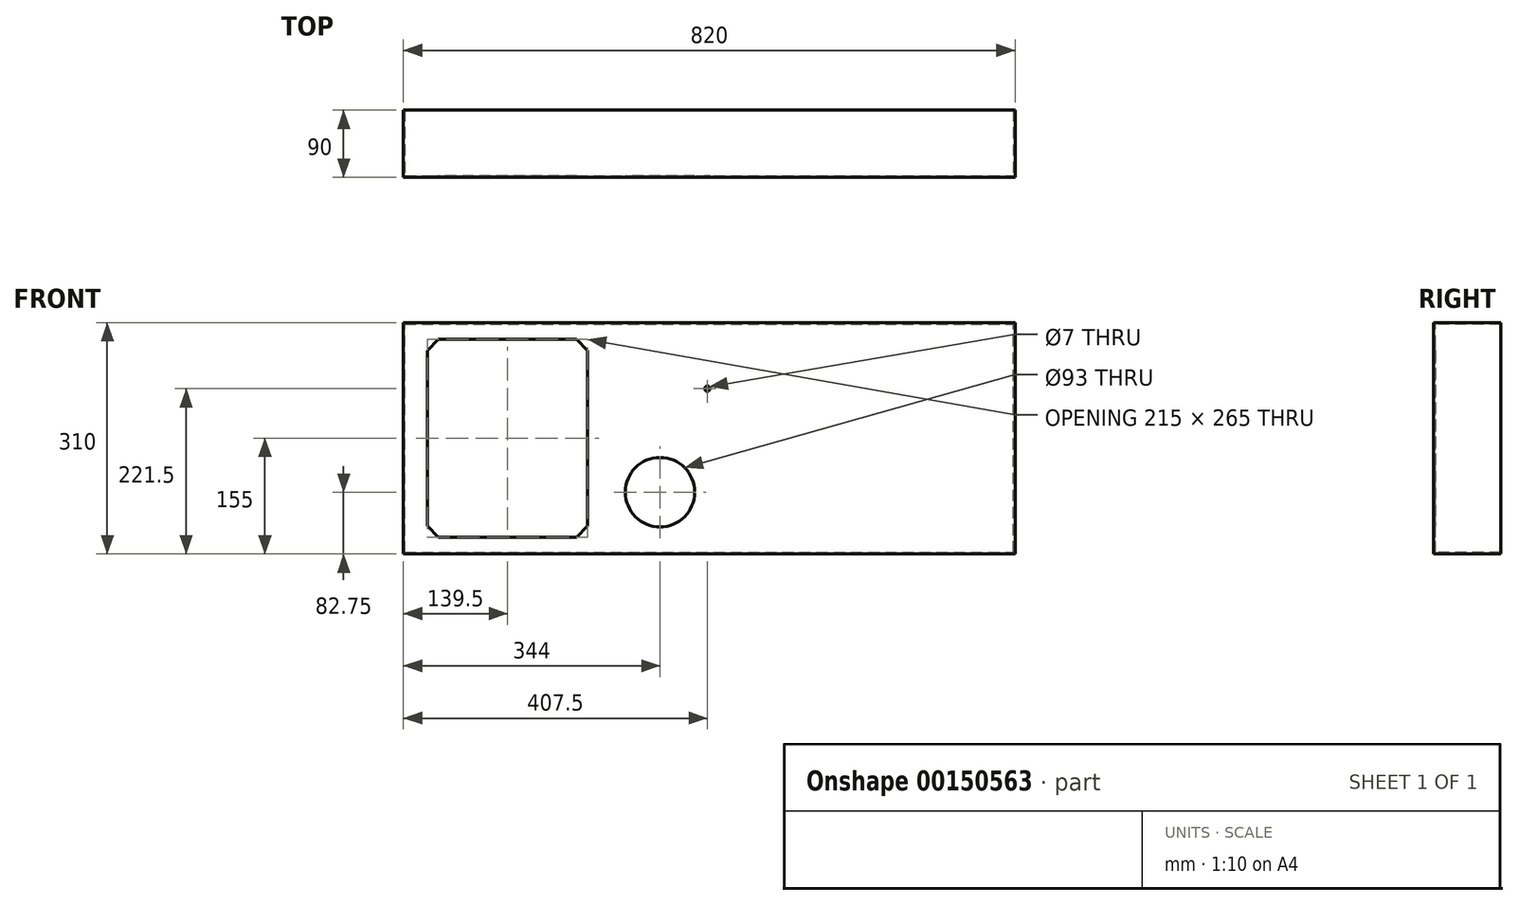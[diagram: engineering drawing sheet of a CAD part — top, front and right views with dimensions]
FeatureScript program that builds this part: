
annotation { "Feature Type Name" : "Feature", "Feature Type Description" : "" }
export const myFeature = defineFeature(function(context is Context, id is Id, definition is map)
    precondition{}
    {
        {
            var Q0;
            Q0=qCreatedBy(makeId("Front.planeOp"),FACE);
            var sketch = newSketch(context, id + "F0", { "sketchPlane" : qUnion([Q0])});
            skLineSegment(sketch, "E0.bottom", {"start": v(0, 0) * mm, "end": v(820, 0) * mm});
            skLineSegment(sketch, "E0.top", {"start": v(0, 310) * mm, "end": v(820, 310) * mm});
            skLineSegment(sketch, "E0.left", {"start": v(0, 0) * mm, "end": v(0, 310) * mm});
            skLineSegment(sketch, "E0.right", {"start": v(820, 0) * mm, "end": v(820, 310) * mm});
            skSolve(sketch);
        }
        {
            var Q0;
            Q0 = qSketchRegion(id + "F0", true);
            extrude(context, id + "F1", {"entities" : qUnion([Q0]), "depth" : 2 * mm});
        }
        {
            var Q0;
            Q0=makeQuery(id+"F1.opExtrude","CAP_FACE",FACE,{"disambiguationData":[OSD([sQuery(id+"F0.wireOp",EDGE,"E0.bottom"),sQuery(id+"F0.wireOp",EDGE,"E0.top"),sQuery(id+"F0.wireOp",EDGE,"E0.left"),sQuery(id+"F0.wireOp",EDGE,"E0.right")])],"isStart":true});
            var sketch = newSketch(context, id + "F2", { "sketchPlane" : qUnion([Q0])});
            skLineSegment(sketch, "E1.0", {"start": v(-820, 0) * mm, "end": v(-820, 310) * mm});
            skLineSegment(sketch, "E1.1", {"start": v(0, 310) * mm, "end": v(-820, 310) * mm});
            skLineSegment(sketch, "E1.2", {"start": v(0, 0) * mm, "end": v(-820, 0) * mm});
            skLineSegment(sketch, "E1.3", {"start": v(0, 0) * mm, "end": v(0, 310) * mm});
            skLineSegment(sketch, "E2.0", {"start": v(-818, 2) * mm, "end": v(-818, 308) * mm});
            skLineSegment(sketch, "E2.1", {"start": v(-2, 2) * mm, "end": v(-818, 2) * mm});
            skLineSegment(sketch, "E2.2", {"start": v(-2, 2) * mm, "end": v(-2, 308) * mm});
            skLineSegment(sketch, "E2.3", {"start": v(-2, 308) * mm, "end": v(-818, 308) * mm});
            skSolve(sketch);
        }
        {
            var Q0;
            Q0 = qSketchRegion(id + "F2", true);
            extrude(context, id + "F3", {"entities" : qUnion([Q0]), "operationType" : NewBodyOperationType.ADD, "depth" : 88 * mm});
        }
        {
            var Q0;
            Q0=makeQuery(id+"F1.opExtrude","CAP_FACE",FACE,{"disambiguationData":[OSD([sQuery(id+"F0.wireOp",EDGE,"E0.bottom"),sQuery(id+"F0.wireOp",EDGE,"E0.top"),sQuery(id+"F0.wireOp",EDGE,"E0.left"),sQuery(id+"F0.wireOp",EDGE,"E0.right")])],"isStart":false});
            var sketch = newSketch(context, id + "F4", { "sketchPlane" : qUnion([Q0])});
            skLineSegment(sketch, "E3", {"start": v(820, 310) * mm, "end": v(820, 0) * mm});
            skLineSegment(sketch, "E4", {"start": v(787, 20) * mm, "end": v(667, 20) * mm});
            skLineSegment(sketch, "E5", {"start": v(667, 20) * mm, "end": v(667, 195) * mm});
            skLineSegment(sketch, "E6", {"start": v(667, 195) * mm, "end": v(787, 195) * mm});
            skLineSegment(sketch, "E7", {"start": v(787, 195) * mm, "end": v(787, 20) * mm});
            skLineSegment(sketch, "E8", {"start": v(818, 2) * mm, "end": v(818, 308) * mm});
            skLineSegment(sketch, "E9", {"start": v(0, 0) * mm, "end": v(0, 310) * mm});
            skLineSegment(sketch, "E10", {"start": v(0, 310) * mm, "end": v(820, 310) * mm});
            skLineSegment(sketch, "E11", {"start": v(820, 0) * mm, "end": v(0, 0) * mm});
            skLineSegment(sketch, "E12", {"start": v(540, 20) * mm, "end": v(540, 100) * mm});
            skLineSegment(sketch, "E13", {"start": v(540, 100) * mm, "end": v(620, 20) * mm});
            skLineSegment(sketch, "E14", {"start": v(620, 20) * mm, "end": v(540, 20) * mm});
            skLineSegment(sketch, "E15", {"start": v(232, 22.5) * mm, "end": v(47, 22.5) * mm});
            skLineSegment(sketch, "E16", {"start": v(32, 37.5) * mm, "end": v(32, 272.5) * mm});
            skLineSegment(sketch, "E17", {"start": v(47, 287.5) * mm, "end": v(232, 287.5) * mm});
            skLineSegment(sketch, "E18", {"start": v(247, 272.5) * mm, "end": v(247, 37.5) * mm});
            skLineSegment(sketch, "E19", {"start": v(232, 22.5) * mm, "end": v(247, 37.5) * mm});
            skLineSegment(sketch, "E20", {"start": v(47, 22.5) * mm, "end": v(32, 37.5) * mm});
            skLineSegment(sketch, "E21", {"start": v(32, 272.5) * mm, "end": v(47, 287.5) * mm});
            skLineSegment(sketch, "E22", {"start": v(247, 272.5) * mm, "end": v(232, 287.5) * mm});
            skLineSegment(sketch, "E23", {"start": v(330, 166.5) * mm, "end": v(262, 166.5) * mm});
            skLineSegment(sketch, "E24", {"start": v(262, 166.5) * mm, "end": v(262, 272.5) * mm});
            skLineSegment(sketch, "E25", {"start": v(262, 272.5) * mm, "end": v(330, 272.5) * mm});
            skLineSegment(sketch, "E26", {"start": v(330, 272.5) * mm, "end": v(330, 166.5) * mm});
            skCircle(sketch, "E27", {"center": v(344, 82.75) * mm, "radius": 46.5 * mm});
            skCircle(sketch, "E28", {"center": v(407.5, 221.5) * mm, "radius": 15.9 * mm});
            skLineSegment(sketch, "E29", {"start": v(2, 2) * mm, "end": v(818, 2) * mm});
            skLineSegment(sketch, "E30", {"start": v(818, 308) * mm, "end": v(2, 308) * mm});
            skLineSegment(sketch, "E31", {"start": v(2, 308) * mm, "end": v(2, 2) * mm});
            skSolve(sketch);
        }
        {
            var Q0;
            Q0=makeQuery(id+"F4.imprint","IMPRINT",FACE,{"disambiguationData":[TD([[makeQuery(id+"F4.imprint","IMPRINT",EDGE,{"derivedFrom":sQuery(id+"F4.wireOp",EDGE,"E4")}),1.0]])]});
            var sketch = newSketch(context, id + "F5", { "sketchPlane" : qUnion([Q0])});
            skLineSegment(sketch, "E32.0", {"start": v(32, 272.5) * mm, "end": v(47, 287.5) * mm});
            skLineSegment(sketch, "E32.1", {"start": v(47, 287.5) * mm, "end": v(232, 287.5) * mm});
            skLineSegment(sketch, "E32.2", {"start": v(32, 37.5) * mm, "end": v(32, 272.5) * mm});
            skLineSegment(sketch, "E32.3", {"start": v(47, 22.5) * mm, "end": v(32, 37.5) * mm});
            skLineSegment(sketch, "E32.4", {"start": v(232, 22.5) * mm, "end": v(47, 22.5) * mm});
            skLineSegment(sketch, "E32.5", {"start": v(232, 22.5) * mm, "end": v(247, 37.5) * mm});
            skLineSegment(sketch, "E32.6", {"start": v(247, 272.5) * mm, "end": v(247, 37.5) * mm});
            skLineSegment(sketch, "E32.7", {"start": v(247, 272.5) * mm, "end": v(232, 287.5) * mm});
            skCircle(sketch, "E33.0", {"center": v(344, 82.75) * mm, "radius": 46.5 * mm});
            skCircle(sketch, "E34", {"center": v(407.5, 221.5) * mm, "radius": 3.5 * mm});
            skSolve(sketch);
        }
        {
            var Q0;
            Q0 = qSketchRegion(id + "F5", true);
            extrude(context, id + "F6", {"entities" : qUnion([Q0]), "operationType" : NewBodyOperationType.REMOVE, "endBound" : BoundingType.THROUGH_ALL, "oppositeDirection" : true, "depth" : 25 * mm});
        }
    });
